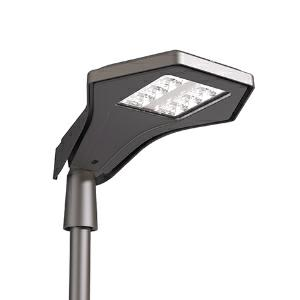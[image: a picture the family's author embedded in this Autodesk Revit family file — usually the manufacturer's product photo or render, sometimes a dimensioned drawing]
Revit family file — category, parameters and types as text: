
# Revit family: 3f_filippi_-_3f_manta_medio_3f_filippi_-_7012_-_3f_manta_an_135-730_medium
name_source: partatom
category: Lighting Fixtures
units: mm (PartAtom-declared; Revit-internal decimal feet)

## family parameters
Cut with Voids When Loaded = No
Host = Face
Light Source = No
Part Type = Normal
Room Calculation Point = No
Round Connector Dimension = Use Diameter
Shared = No

## types (1)
- 3F Filippi - 3F Manta Medio (1 x LED, 17360 lm, 149 W, 3000 K)
    Apparent Load = 149 VA
    Approval mark = CE
    CIE Flux Codes = 40 79 99 100 100
    Color Rendering = 70
    Color Temperature = 3000 K
    Control Gear = Electronic ballast
    Default Elevation = 1800 mm
    Description = ILLUMINOTECHNICAL
Luminous efficiency 100% (DLOR 100%, ULOR 0%).
Initial luminous flux of the luminaire 17360 lm.
Asymmetric distribution with medium bilateral.
BUG (Backlight, Uplight, Glare) IESNA TM-15: B3 U0 G2.
Beam angle: 141° - 69°.
Luminous efficacy 117 lm/W.
Lifetime (L93/B10): 30000 h. (tq+25°C)
Lifetime (L90/B10): 50000 h. (tq+25°C)
Lifetime (L85/B10): 80000 h. (tq+25°C)
Lifetime (L80/B10): 100000 h. (tq+25°C)
Lifetime (L90/B20): 50000 h. (tq+45°C)
Sudden decreased luminous flux after 50000 hours: 0% (C0).
Photobiological safety in compliance with IEC/TR 62778: RG0 risk exempt, (IEC 62471).
In compliance with IEC/EN 62722-2-1 - IEC/EN 62717 standards.

SOURCE
Squared LED module 135W/730.
Source with special protection against aggressive chemically-volatile substances for standard LED technology.
Energy efficiency class (UE 2019/2020 - UE 2019/2015): E.
CIE 13.3 Colour rendering index: CRI >70 (R9 <50%).
IES TM-30 Fidelity Index: Rf = 72 Rg = 95.
CCT nominal colour temperature 3000 K.
Colour initial tolerance (MacAdam): SDCM 5.

MECHANICAL
Aerodynamically-shaped die-cast aluminium double-shell body for low wind resistance (frontal: 0.0446 m²; lateral: 0.0505 m²), equipped with fins to optimize the cooling of the internal components.
Shell closure using stainless steel screws on stainless steel bushings, with hinged opening for easy access to the wiring compartment, equipped with system against accidental closure.
Polyester powder coating with degreasing pre-treatment and phosphate layer deposit on the metal, UV stabilised, corrosion resistant, anthracite colour, salt spray resistance ISO 9227 >1000 h.
Parabolic cellular optics with total recovery, entirely made of semi-specular high reflection aluminium with titanium and magnesium surface treatment, to maintain optical performance over time.
Polyurethane foam seals, ecological, anti-aging, installed using a continuous automatic process with no joints.
VT extra transparent tempered glass diffuser, 4 mm thick, non-combustible, with Heat Soak Test (HST) thermal treatment, which drastically reduces the risk of spontaneous breakage.
Stainless steel internal and external screws.
Luminaire with limited surface temperature. - D - (EN 60598-2-24)
Dimensions: 660x440 mm, height 166 mm. Weight 11.5 kg.
IP66 protection degree.
Mechanical strength to impacts IK08 (5 joule).
Glow-wire test resistance 960°C.

ELECTRICAL
Halogen Free electronic wiring 230V-50/60Hz, power factor 0.97, THD <25%, constant output current, class I, 1 driver.
Power of the luminaire 149 W.
ENEC - CE.
Flicker: <5%.
Ambient temperature from -20°C to +45°C.
Temperature class T6 max 85°C.
Safety break switch to shut off the power supply when opening the device.
Insulation voltage 6kV via Sourge Protector.
SPD type 2+3 (combined) device to protect against voltage surges up to 10 kV in common and differential mode.
Thermal protection of the LED module via NTC sensor (Negative Temperature Coefficient).
M20x1.5 IP68 nylon cable gland for feeding input (cables with an min-max diameter 6-13mm).
Pressure compensating valve with anti-condensation effect.
Relative humidity UR: <85%.

INSTALLATION
Post-top / arm / wall.
Installation with always necessary "Pole fixing" accessory (see accessories).
All accessories dedicated to this product are available on the Catalog and on our website www.3F-Filippi.com.

ACCESSORIES
Pole mount in die-cast aluminium with the same paint treatment as the body (for Ø 60 mm and Ø 76 mm poles) equipped with special teeth for adjusting the inclination on the head of the device by ± 20° with an adjustment pitch of 5°.
Possibility of installing on vertical pole (pole head) and horizontal pole (arm).
Mounting on the device using the supplied stainless steel screws on self-locking stainless steel nuts.
A0439 - Pole mounting diameter 60 mm.
A0440 - Pole mounting diameter 76 mm.

APPLICATIONS
Outdoor environments, general lighting, work and roadway lighting, transit areas and building perimeters, parking lots, trade fairs.
Control of light pollution, in accordance with the legislative requirements in force.

LIGHT MANAGEMENT
Upon request, the appliance can be supplied with "Virtual Midnight" programming.

WARNING
Luminaire designed for disposal/recycling at end-of-life.
Replaceable (LED only) light source by a professional. Replaceable control gear by a professional.
    Height = 166 mm
    Lamp = 1 x LED
    Lamp Light Flux = 17360 lm
    Lamp Power = 149 W
    Lamp count = 1
    Length = 660 mm
    Lifetime = 50000 h
    Luminous efficacy = 117 lm/W
    Manufacturer = 3F Filippi
    ModVariant = No
    Model = 3F Filippi - 7012 - 3F Manta AN 135-730 MEDIUM
    Mounting Place = Pole
    Mounting Type = Pole top
    Number of Poles = 1
    OnlyDefault = Yes
    Power Factor = 1
    Product Name = 3F Filippi - 3F Manta Medio
    Product group = street luminaire
    ProductGroupID = 15
    Protection Class = Protection class I
    Protection Degree = IP 66
    RLX_Detail_Level = 1
    RLX_Emergency_Light_Flux = 0 lm
    RLX_Emergency_Type = 0
    RLX_Emergency_Type_DB = No
    RlxData = <blob elided: 224701 chars, md5=46eddca4>
    Socket = socket
    Standby Power = 0 W
    System Light Flux = 17360 lm
    System Power = 149 W
    Type Comments = Product without accessories
    Type Image = 3ffilippi_3f_manta_medium.jpg
    URL = http://relux.com
    VarID = ---
    Voltage = 0 V
    Weight = 0.00 kg
    Width = 440 mm

## geometry (parser evidence)
native form markers: Blend x4, Sweep x12
no freeform markers — native parametric forms only
